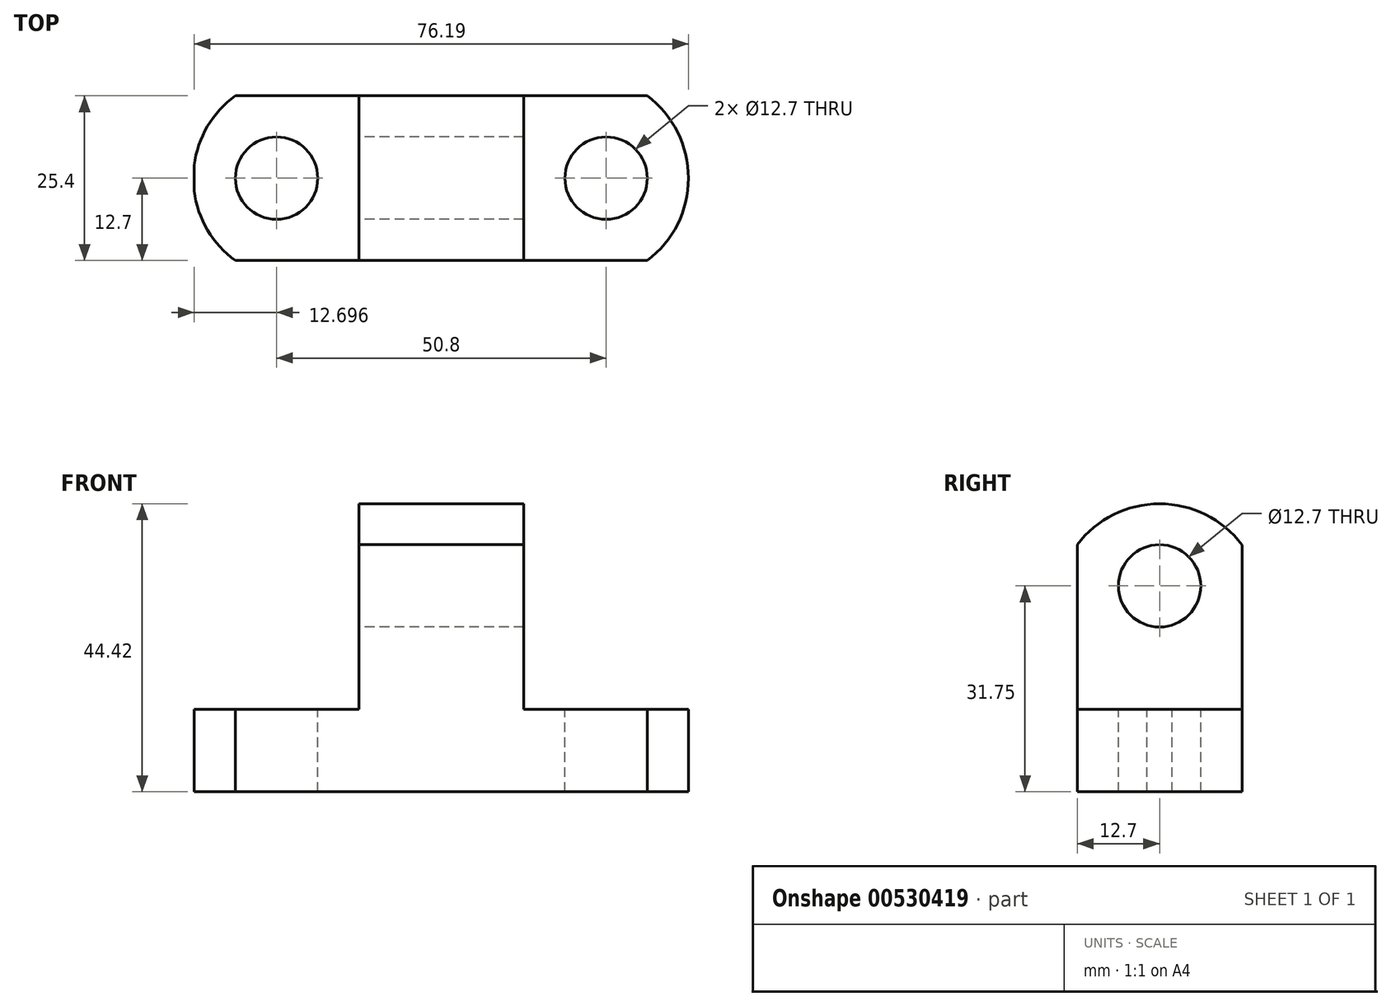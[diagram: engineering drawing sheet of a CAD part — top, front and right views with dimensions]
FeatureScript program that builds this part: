
annotation { "Feature Type Name" : "Feature", "Feature Type Description" : "" }
export const myFeature = defineFeature(function(context is Context, id is Id, definition is map)
    precondition{}
    {
        {
            var Q0;
            Q0=qCreatedBy(makeId("Front.planeOp"),FACE);
            var sketch = newSketch(context, id + "F0", { "sketchPlane" : qUnion([Q0])});
            skLineSegment(sketch, "E0", {"start": v(-51.84, 0) * mm, "end": v(24.36, 0) * mm});
            skLineSegment(sketch, "E1", {"start": v(24.36, 0) * mm, "end": v(24.36, 12.7) * mm});
            skLineSegment(sketch, "E2", {"start": v(24.36, 12.7) * mm, "end": v(-1.04, 12.7) * mm});
            skLineSegment(sketch, "E3", {"start": v(-1.04, 12.7) * mm, "end": v(-1.04, 44.45) * mm});
            skLineSegment(sketch, "E4", {"start": v(-1.04, 44.45) * mm, "end": v(-26.44, 44.45) * mm});
            skLineSegment(sketch, "E5", {"start": v(-26.44, 44.45) * mm, "end": v(-26.44, 12.7) * mm});
            skLineSegment(sketch, "E6", {"start": v(-26.44, 12.7) * mm, "end": v(-51.84, 12.7) * mm});
            skLineSegment(sketch, "E7", {"start": v(-51.84, 12.7) * mm, "end": v(-51.84, 0) * mm});
            skSolve(sketch);
        }
        {
            var Q0;
            Q0=makeQuery(id+"F0.imprint","IMPRINT",FACE,{"disambiguationData":[TD([[makeQuery(id+"F0.imprint","IMPRINT",EDGE,{"derivedFrom":sQuery(id+"F0.wireOp",EDGE,"E0")}),1.0]])]});
            extrude(context, id + "F1", {"entities" : qUnion([Q0]), "depth" : 25.4 * mm, "offsetDistance" : 25.4 * mm});
        }
        {
            var Q0;
            Q0=makeQuery(id+"F1.opExtrude","SWEPT_FACE",FACE,{"disambiguationData":[OSD([sQuery(id+"F0.wireOp",EDGE,"E5")])]});
            var sketch = newSketch(context, id + "F2", { "sketchPlane" : qUnion([Q0])});
            skArc(sketch, "E8", {"start": v(25.4, 37.26) * mm, "mid": v(12.75, 44.1) * mm, "end": v(0, 37.47) * mm});
            skCircle(sketch, "E9", {"center": v(12.7, 31.75) * mm, "radius": 6.35 * mm});
            skSolve(sketch);
        }
        {
            var Q0;
            Q0=makeQuery(id+"F2.imprint","IMPRINT",FACE,{"disambiguationData":[TD([[makeQuery(id+"F2.imprint","IMPRINT",EDGE,{"derivedFrom":sQuery(id+"F2.wireOp",EDGE,"E9")}),1.0]])]});
            extrude(context, id + "F3", {"entities" : qUnion([Q0]), "operationType" : NewBodyOperationType.REMOVE, "endBound" : BoundingType.THROUGH_ALL, "oppositeDirection" : true, "depth" : 25.4 * mm, "offsetDistance" : 25.4 * mm});
        }
        {
            var Q0;
            Q0=makeQuery(id+"F1.opExtrude","SWEPT_FACE",FACE,{"disambiguationData":[OSD([sQuery(id+"F0.wireOp",EDGE,"E3")])]});
            var sketch = newSketch(context, id + "F4", { "sketchPlane" : qUnion([Q0])});
            skArc(sketch, "E10", {"start": v(0, 38.1) * mm, "mid": v(-12.7, 44.42) * mm, "end": v(-25.4, 38.1) * mm});
            skSolve(sketch);
        }
        {
            var Q0;
            {var subQ0=sQuery(id+"F4.wireOp",EDGE,"E10");Q0=makeQuery(id+"F4.imprint","IMPRINT",FACE,{"disambiguationData":[TD([[makeQuery(id+"F4.imprint","IMPRINT",EDGE,{"derivedFrom":subQ0}),-1.0]])]});}
            extrude(context, id + "F5", {"entities" : qUnion([Q0]), "operationType" : NewBodyOperationType.REMOVE, "endBound" : BoundingType.THROUGH_ALL, "oppositeDirection" : true, "depth" : 25.4 * mm, "offsetDistance" : 25.4 * mm});
        }
        {
            var Q0;
            Q0=makeQuery(id+"F1.opExtrude","SWEPT_FACE",FACE,{"disambiguationData":[OSD([sQuery(id+"F0.wireOp",EDGE,"E6")])]});
            var sketch = newSketch(context, id + "F6", { "sketchPlane" : qUnion([Q0])});
            skCircle(sketch, "E11", {"center": v(-39.14, -12.7) * mm, "radius": 6.35 * mm});
            skCircle(sketch, "E12", {"center": v(11.66, -12.7) * mm, "radius": 6.35 * mm});
            skSolve(sketch);
        }
        {
            var Q0;
            Q0=makeQuery(id+"F6.imprint","IMPRINT",FACE,{"disambiguationData":[TD([[makeQuery(id+"F6.imprint","IMPRINT",EDGE,{"derivedFrom":sQuery(id+"F6.wireOp",EDGE,"E11")}),1.0]])]});
            var Q1;
            Q1=makeQuery(id+"F6.imprint","IMPRINT",FACE,{"disambiguationData":[TD([[makeQuery(id+"F6.imprint","IMPRINT",EDGE,{"derivedFrom":sQuery(id+"F6.wireOp",EDGE,"E12")}),1.0]])]});
            extrude(context, id + "F7", {"entities" : qUnion([Q0, Q1]), "operationType" : NewBodyOperationType.REMOVE, "endBound" : BoundingType.THROUGH_ALL, "oppositeDirection" : true, "depth" : 25.4 * mm, "offsetDistance" : 25.4 * mm});
        }
        {
            var Q0;
            Q0=makeQuery(id+"F1.opExtrude","SWEPT_FACE",FACE,{"disambiguationData":[OSD([sQuery(id+"F0.wireOp",EDGE,"E6")])]});
            var sketch = newSketch(context, id + "F8", { "sketchPlane" : qUnion([Q0])});
            skArc(sketch, "E13", {"start": v(-45.5, 0) * mm, "mid": v(-51.97, -12.7) * mm, "end": v(-45.5, -25.4) * mm});
            skSolve(sketch);
        }
        {
            var Q0;
            {var subQ0=sQuery(id+"F8.wireOp",EDGE,"E13");var subQ1=sQuery(id+"F0.wireOp",EDGE,"E6");var subQ2=makeQuery(id+"F1.opExtrude","CAP_EDGE",EDGE,{"disambiguationData":[OSD([subQ1])],"isStart":false});var subQ3=makeQuery(id+"F8.imprint","INTERSECT",VERTEX,{"derivedFrom":[subQ2,subQ0]});Q0=makeQuery(id+"F8.imprint","IMPRINT",FACE,{"disambiguationData":[TD([[makeQuery(id+"F8.imprint","IMPRINT",EDGE,{"disambiguationData":[TD([[subQ3,1.0]])],"derivedFrom":subQ0}),-1.0]])]});}
            var Q1;
            {var subQ0=sQuery(id+"F8.wireOp",EDGE,"E13");var subQ1=sQuery(id+"F0.wireOp",EDGE,"E6");var subQ2=makeQuery(id+"F1.opExtrude","CAP_EDGE",EDGE,{"disambiguationData":[OSD([subQ1])],"isStart":true});var subQ3=makeQuery(id+"F8.imprint","INTERSECT",VERTEX,{"derivedFrom":[subQ2,subQ0]});Q1=makeQuery(id+"F8.imprint","IMPRINT",FACE,{"disambiguationData":[TD([[makeQuery(id+"F8.imprint","IMPRINT",EDGE,{"disambiguationData":[TD([[subQ3,-1.0]])],"derivedFrom":subQ0}),-1.0]])]});}
            extrude(context, id + "F9", {"entities" : qUnion([Q0, Q1]), "operationType" : NewBodyOperationType.REMOVE, "endBound" : BoundingType.THROUGH_ALL, "oppositeDirection" : true, "depth" : 25.4 * mm, "offsetDistance" : 25.4 * mm});
        }
        {
            var Q0;
            Q0=makeQuery(id+"F1.opExtrude","SWEPT_FACE",FACE,{"disambiguationData":[OSD([sQuery(id+"F0.wireOp",EDGE,"E2")])]});
            var sketch = newSketch(context, id + "F10", { "sketchPlane" : qUnion([Q0])});
            skArc(sketch, "E14", {"start": v(18, -25.4) * mm, "mid": v(24.35, -12.7) * mm, "end": v(18, 0) * mm});
            skSolve(sketch);
        }
        {
            var Q0;
            {var subQ0=sQuery(id+"F10.wireOp",EDGE,"E14");Q0=makeQuery(id+"F10.imprint","IMPRINT",FACE,{"disambiguationData":[TD([[makeQuery(id+"F10.imprint","IMPRINT",EDGE,{"derivedFrom":subQ0}),-1.0]])]});}
            extrude(context, id + "F11", {"entities" : qUnion([Q0]), "operationType" : NewBodyOperationType.REMOVE, "endBound" : BoundingType.THROUGH_ALL, "oppositeDirection" : true, "depth" : 25.4 * mm, "offsetDistance" : 25.4 * mm});
        }
    });
